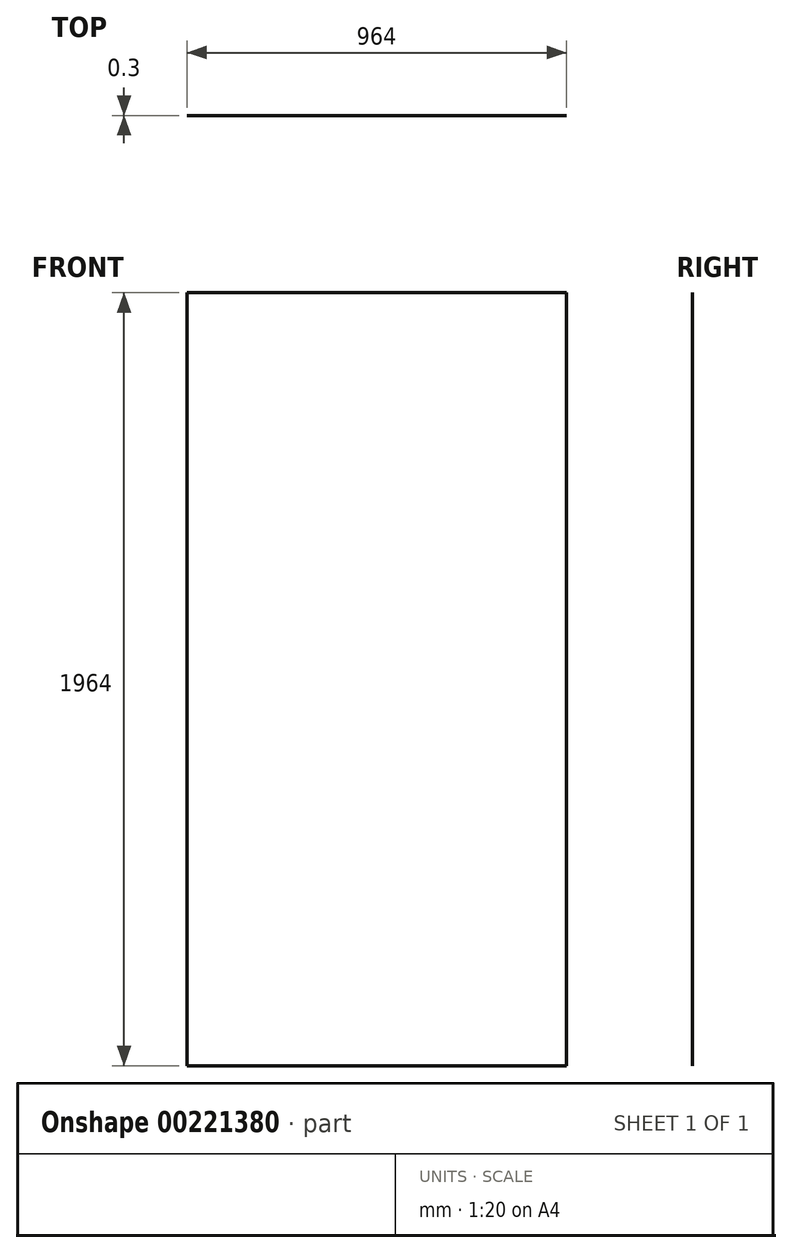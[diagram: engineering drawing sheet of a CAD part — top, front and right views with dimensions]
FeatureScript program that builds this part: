
annotation { "Feature Type Name" : "Feature", "Feature Type Description" : "" }
export const myFeature = defineFeature(function(context is Context, id is Id, definition is map)
    precondition{}
    {
        {
            var Q0;
            Q0=qCreatedBy(makeId("Front.planeOp"),FACE);
            var sketch = newSketch(context, id + "F0", { "sketchPlane" : qUnion([Q0])});
            skLineSegment(sketch, "E0.bottom", {"start": v(482, -982) * mm, "end": v(-482, -982) * mm});
            skLineSegment(sketch, "E0.top", {"start": v(482, 982) * mm, "end": v(-482, 982) * mm});
            skLineSegment(sketch, "E0.left", {"start": v(482, -982) * mm, "end": v(482, 982) * mm});
            skLineSegment(sketch, "E0.right", {"start": v(-482, -982) * mm, "end": v(-482, 982) * mm});
            skPoint(sketch, "E0.middle", {"position": v(0, 0) * mm});
            skSolve(sketch);
        }
        {
            var Q0;
            Q0=qSketchRegion(id+"F0",true);
            extrude(context, id + "F1", {"entities" : qUnion([Q0]), "depth" : 0.3 * mm});
        }
    });
